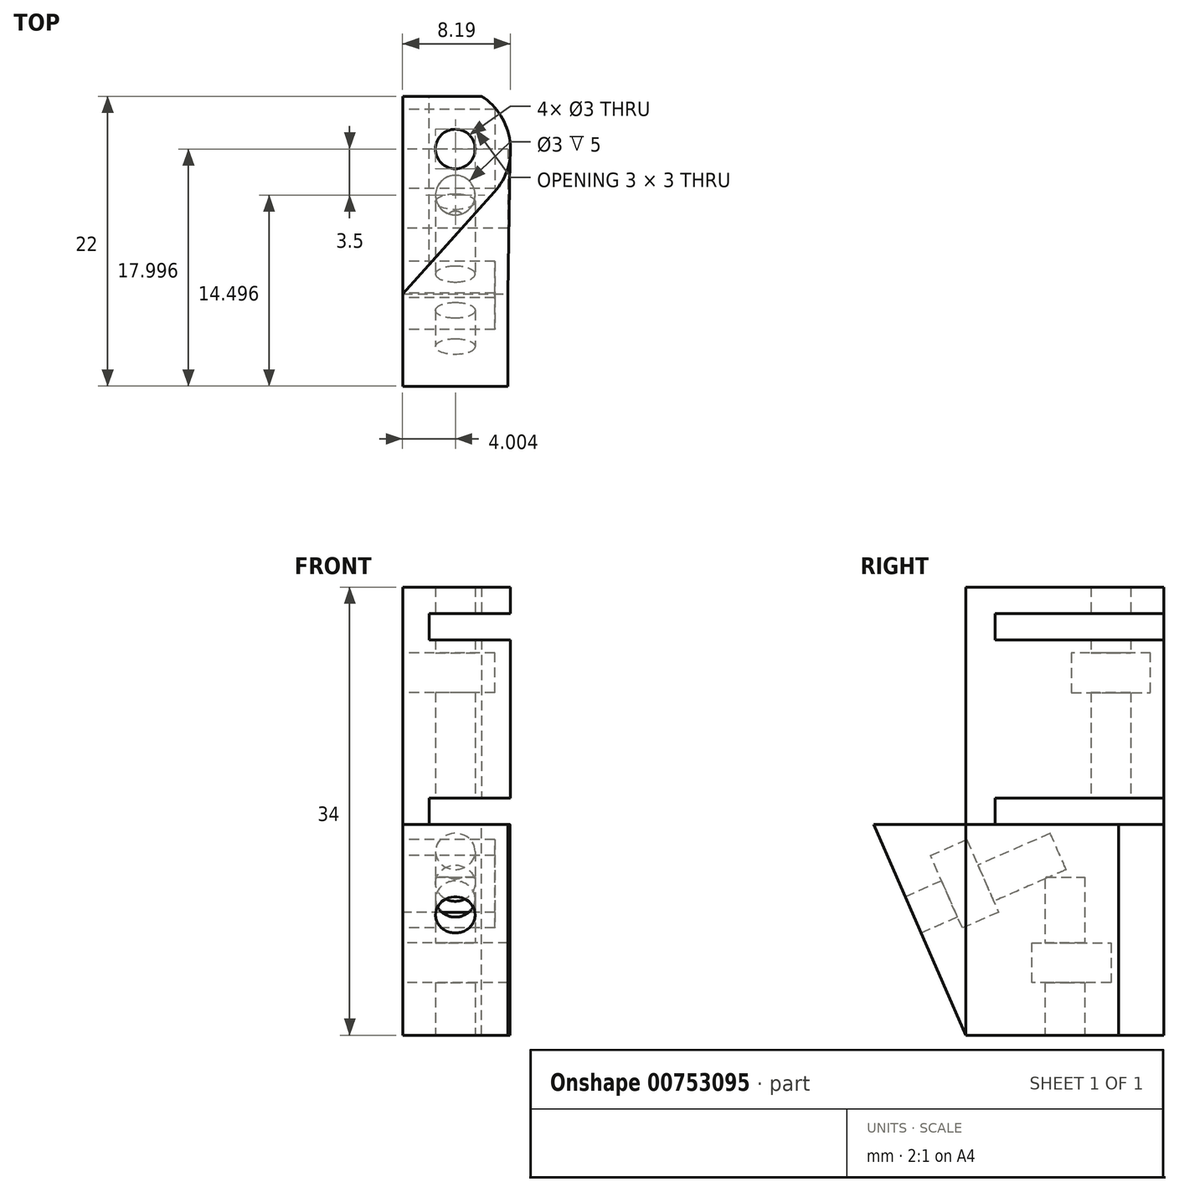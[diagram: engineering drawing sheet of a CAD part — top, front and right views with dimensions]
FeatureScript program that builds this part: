
annotation { "Feature Type Name" : "Feature", "Feature Type Description" : "" }
export const myFeature = defineFeature(function(context is Context, id is Id, definition is map)
    precondition{}
    {
        {
            var Q0;
            Q0=qCreatedBy(makeId("Top.planeOp"),FACE);
            var sketch = newSketch(context, id + "F0", { "sketchPlane" : qUnion([Q0])});
            skLineSegment(sketch, "E0", {"start": v(-26.19, -5.95) * mm, "end": v(-26.19, -20.95) * mm});
            skLineSegment(sketch, "E1", {"start": v(-26.19, -5.95) * mm, "end": v(-20.2, -5.95) * mm});
            skLineSegment(sketch, "E2", {"start": v(-26.19, -20.95) * mm, "end": v(-26.19, -14.95) * mm});
            skLineSegment(sketch, "E3", {"start": v(-26.19, -20.95) * mm, "end": v(-19.23, -13.23) * mm});
            skArc(sketch, "E4", {"start": v(-19.23, -13.23) * mm, "mid": v(-18.04, -9.37) * mm, "end": v(-20.2, -5.95) * mm});
            skCircle(sketch, "E5", {"center": v(-22.19, -9.95) * mm, "radius": 1.5 * mm});
            skSolve(sketch);
        }
        {
            var Q0;
            Q0=makeQuery(id+"F0.imprint","IMPRINT",FACE,{"disambiguationData":[TD([[makeQuery(id+"F0.imprint","IMPRINT",EDGE,{"derivedFrom":sQuery(id+"F0.wireOp",EDGE,"E0")}),1.0]])]});
            extrude(context, id + "F1", {"entities" : qUnion([Q0]), "depth" : 18 * mm, "offsetDistance" : 25 * mm});
        }
        {
            var Q0;
            Q0=makeQuery(id+"F1.opExtrude","SWEPT_FACE",FACE,{"disambiguationData":[OSD([sQuery(id+"F0.wireOp",EDGE,"E0"),sQuery(id+"F0.wireOp",EDGE,"E2")])]});
            var sketch = newSketch(context, id + "F2", { "sketchPlane" : qUnion([Q0])});
            skLineSegment(sketch, "E6", {"start": v(6.95, 13) * mm, "end": v(12.95, 13) * mm});
            skLineSegment(sketch, "E7", {"start": v(12.95, 13) * mm, "end": v(12.95, 10) * mm});
            skLineSegment(sketch, "E8", {"start": v(12.95, 10) * mm, "end": v(6.95, 10) * mm});
            skLineSegment(sketch, "E9", {"start": v(6.95, 10) * mm, "end": v(6.95, 13) * mm});
            skSolve(sketch);
        }
        {
            var Q0;
            Q0=makeQuery(id+"F2.imprint","IMPRINT",FACE,{"disambiguationData":[TD([[makeQuery(id+"F2.imprint","IMPRINT",EDGE,{"derivedFrom":sQuery(id+"F2.wireOp",EDGE,"E6")}),-1.0]])]});
            extrude(context, id + "F3", {"entities" : qUnion([Q0]), "operationType" : NewBodyOperationType.REMOVE, "oppositeDirection" : true, "depth" : 7 * mm, "offsetDistance" : 25 * mm});
        }
        {
            var Q0;
            Q0=makeQuery(id+"F1.opExtrude","CAP_FACE",FACE,{"disambiguationData":[OSD([sQuery(id+"F0.wireOp",EDGE,"E0"),sQuery(id+"F0.wireOp",EDGE,"E1"),sQuery(id+"F0.wireOp",EDGE,"E2"),sQuery(id+"F0.wireOp",EDGE,"E3"),sQuery(id+"F0.wireOp",EDGE,"E4"),sQuery(id+"F0.wireOp",EDGE,"E5")])],"isStart":true});
            var sketch = newSketch(context, id + "F4", { "sketchPlane" : qUnion([Q0])});
            skLineSegment(sketch, "E10", {"start": v(-26.19, 20.95) * mm, "end": v(-18.19, 20.95) * mm});
            skPoint(sketch, "E11.endSnap0", {"position": v(-18.04, 9.37) * mm});
            skLineSegment(sketch, "E12", {"start": v(-26.19, 20.95) * mm, "end": v(-26.19, 5.95) * mm});
            skLineSegment(sketch, "E13", {"start": v(-26.19, 5.95) * mm, "end": v(-20.2, 5.95) * mm});
            skArc(sketch, "E14", {"start": v(-20.2, 5.95) * mm, "mid": v(-18.74, 7.43) * mm, "end": v(-18.04, 9.37) * mm});
            skLineSegment(sketch, "E15", {"start": v(-18.19, 20.95) * mm, "end": v(-18.04, 9.37) * mm});
            skSolve(sketch);
        }
        {
            var Q0;
            Q0=makeQuery(id+"F4.imprint","IMPRINT",FACE,{"disambiguationData":[TD([[makeQuery(id+"F4.imprint","IMPRINT",EDGE,{"derivedFrom":sQuery(id+"F4.wireOp",EDGE,"E12")}),-1.0]])]});
            var Q1;
            {var subQ0=sQuery(id+"F4.wireOp",EDGE,"E10");Q1=makeQuery(id+"F4.imprint","IMPRINT",FACE,{"disambiguationData":[TD([[makeQuery(id+"F4.imprint","IMPRINT",EDGE,{"derivedFrom":subQ0}),-1.0]])]});}
            extrude(context, id + "F5", {"entities" : qUnion([Q0, Q1]), "operationType" : NewBodyOperationType.ADD, "depth" : 16 * mm, "offsetDistance" : 25 * mm});
        }
        {
            var Q0;
            Q0=makeQuery(id+"F5.opExtrude","CAP_FACE",FACE,{"disambiguationData":[OSD([sQuery(id+"F0.wireOp",EDGE,"E5"),sQuery(id+"F4.wireOp",EDGE,"E10"),sQuery(id+"F4.wireOp",EDGE,"E12"),sQuery(id+"F4.wireOp",EDGE,"E13"),sQuery(id+"F4.wireOp",EDGE,"E14"),sQuery(id+"F4.wireOp",EDGE,"E15")])],"isStart":false});
            var sketch = newSketch(context, id + "F6", { "sketchPlane" : qUnion([Q0])});
            skCircle(sketch, "E16", {"center": v(-22.19, 9.95) * mm, "radius": 1.5 * mm});
            skSolve(sketch);
        }
        {
            var Q0;
            Q0=qSketchRegion(id+"F6",true);
            extrude(context, id + "F7", {"entities" : qUnion([Q0]), "operationType" : NewBodyOperationType.ADD, "depth" : -16 * mm, "offsetDistance" : 25 * mm});
        }
        {
            var Q0;
            Q0=makeQuery(id+"F5.boolean.opBoolean","MERGE",FACE,{"derivedFrom":[makeQuery(id+"F1.opExtrude","SWEPT_FACE",FACE,{"disambiguationData":[OSD([sQuery(id+"F0.wireOp",EDGE,"E0"),sQuery(id+"F0.wireOp",EDGE,"E2")])]}),makeQuery(id+"F5.opExtrude","SWEPT_FACE",FACE,{"disambiguationData":[OSD([sQuery(id+"F4.wireOp",EDGE,"E12")])]})]});
            var sketch = newSketch(context, id + "F8", { "sketchPlane" : qUnion([Q0])});
            skLineSegment(sketch, "E17", {"start": v(20.95, -16) * mm, "end": v(20.95, 0) * mm});
            skLineSegment(sketch, "E18", {"start": v(20.95, 0) * mm, "end": v(27.95, 0) * mm});
            skLineSegment(sketch, "E19", {"start": v(27.95, 0) * mm, "end": v(20.95, -16) * mm});
            skSolve(sketch);
        }
        {
            var Q0;
            Q0=makeQuery(id+"F8.imprint","IMPRINT",FACE,{"disambiguationData":[TD([[makeQuery(id+"F8.imprint","IMPRINT",EDGE,{"derivedFrom":sQuery(id+"F8.wireOp",EDGE,"E17")}),-1.0]])]});
            extrude(context, id + "F9", {"entities" : qUnion([Q0]), "operationType" : NewBodyOperationType.ADD, "depth" : -8 * mm, "offsetDistance" : 25 * mm});
        }
        {
            var Q0;
            Q0=makeQuery(id+"F9.boolean.opBoolean","MERGE",FACE,{"derivedFrom":[makeQuery(id+"F5.boolean.opBoolean","MERGE",FACE,{"derivedFrom":[makeQuery(id+"F1.opExtrude","SWEPT_FACE",FACE,{"disambiguationData":[OSD([sQuery(id+"F0.wireOp",EDGE,"E0"),sQuery(id+"F0.wireOp",EDGE,"E2")])]}),makeQuery(id+"F5.opExtrude","SWEPT_FACE",FACE,{"disambiguationData":[OSD([sQuery(id+"F4.wireOp",EDGE,"E12")])]})]}),makeQuery(id+"F9.opExtrude","CAP_FACE",FACE,{"disambiguationData":[OSD([sQuery(id+"F8.wireOp",EDGE,"E17"),sQuery(id+"F8.wireOp",EDGE,"E18"),sQuery(id+"F8.wireOp",EDGE,"E19")])],"isStart":true})]});
            var sketch = newSketch(context, id + "F10", { "sketchPlane" : qUnion([Q0])});
            skLineSegment(sketch, "E20", {"start": v(23.64, -2.37) * mm, "end": v(20.9, -1.17) * mm});
            skLineSegment(sketch, "E21", {"start": v(20.9, -1.17) * mm, "end": v(18.48, -6.66) * mm});
            skLineSegment(sketch, "E22", {"start": v(18.48, -6.66) * mm, "end": v(21.23, -7.87) * mm});
            skLineSegment(sketch, "E23", {"start": v(21.23, -7.87) * mm, "end": v(23.64, -2.37) * mm});
            skSolve(sketch);
        }
        {
            var Q0;
            Q0=makeQuery(id+"F10.imprint","IMPRINT",FACE,{"disambiguationData":[TD([[makeQuery(id+"F10.imprint","IMPRINT",EDGE,{"derivedFrom":sQuery(id+"F10.wireOp",EDGE,"E20")}),1.0]])]});
            extrude(context, id + "F11", {"entities" : qUnion([Q0]), "operationType" : NewBodyOperationType.REMOVE, "oppositeDirection" : true, "depth" : 7 * mm, "offsetDistance" : 25 * mm});
        }
        {
            var Q0;
            Q0=makeQuery(id+"F9.opExtrude","SWEPT_FACE",FACE,{"disambiguationData":[OSD([sQuery(id+"F8.wireOp",EDGE,"E19")])]});
            var sketch = newSketch(context, id + "F12", { "sketchPlane" : qUnion([Q0])});
            skCircle(sketch, "E24", {"center": v(-22.19, 3.7) * mm, "radius": 1.5 * mm});
            skSolve(sketch);
        }
        {
            var Q0;
            Q0=makeQuery(id+"F12.imprint","IMPRINT",FACE,{"disambiguationData":[TD([[makeQuery(id+"F12.imprint","IMPRINT",EDGE,{"derivedFrom":sQuery(id+"F12.wireOp",EDGE,"E24")}),1.0]])]});
            extrude(context, id + "F13", {"entities" : qUnion([Q0]), "operationType" : NewBodyOperationType.REMOVE, "oppositeDirection" : true, "depth" : 12 * mm, "offsetDistance" : 25 * mm});
        }
        {
            var Q0;
            Q0=makeQuery(id+"F9.boolean.opBoolean","MERGE",FACE,{"derivedFrom":[makeQuery(id+"F5.boolean.opBoolean","MERGE",FACE,{"derivedFrom":[makeQuery(id+"F1.opExtrude","SWEPT_FACE",FACE,{"disambiguationData":[OSD([sQuery(id+"F0.wireOp",EDGE,"E0"),sQuery(id+"F0.wireOp",EDGE,"E2")])]}),makeQuery(id+"F5.opExtrude","SWEPT_FACE",FACE,{"disambiguationData":[OSD([sQuery(id+"F4.wireOp",EDGE,"E12")])]})]}),makeQuery(id+"F9.opExtrude","CAP_FACE",FACE,{"disambiguationData":[OSD([sQuery(id+"F8.wireOp",EDGE,"E17"),sQuery(id+"F8.wireOp",EDGE,"E18"),sQuery(id+"F8.wireOp",EDGE,"E19")])],"isStart":true})]});
            var sketch = newSketch(context, id + "F14", { "sketchPlane" : qUnion([Q0])});
            skLineSegment(sketch, "E25", {"start": v(9.95, -12) * mm, "end": v(15.95, -12) * mm});
            skLineSegment(sketch, "E26", {"start": v(15.95, -12) * mm, "end": v(15.95, -9) * mm});
            skLineSegment(sketch, "E27", {"start": v(15.95, -9) * mm, "end": v(9.95, -9) * mm});
            skLineSegment(sketch, "E28", {"start": v(9.95, -9) * mm, "end": v(9.95, -12) * mm});
            skSolve(sketch);
        }
        {
            var Q0;
            Q0=makeQuery(id+"F14.imprint","IMPRINT",FACE,{"disambiguationData":[TD([[makeQuery(id+"F14.imprint","IMPRINT",EDGE,{"derivedFrom":sQuery(id+"F14.wireOp",EDGE,"E25")}),1.0]])]});
            extrude(context, id + "F15", {"entities" : qUnion([Q0]), "operationType" : NewBodyOperationType.REMOVE, "oppositeDirection" : true, "depth" : 8 * mm, "offsetDistance" : 25 * mm});
        }
        {
            var Q0;
            Q0=makeQuery(id+"F7.boolean.opBoolean","MERGE",FACE,{"derivedFrom":[makeQuery(id+"F5.opExtrude","CAP_FACE",FACE,{"disambiguationData":[OSD([sQuery(id+"F0.wireOp",EDGE,"E5"),sQuery(id+"F4.wireOp",EDGE,"E10"),sQuery(id+"F4.wireOp",EDGE,"E12"),sQuery(id+"F4.wireOp",EDGE,"E13"),sQuery(id+"F4.wireOp",EDGE,"E14"),sQuery(id+"F4.wireOp",EDGE,"E15")])],"isStart":false}),makeQuery(id+"F7.opExtrude","CAP_FACE",FACE,{"disambiguationData":[OSD([sQuery(id+"F6.wireOp",EDGE,"E16")])],"isStart":true})]});
            var sketch = newSketch(context, id + "F16", { "sketchPlane" : qUnion([Q0])});
            skCircle(sketch, "E29", {"center": v(-22.19, 13.45) * mm, "radius": 1.5 * mm});
            skSolve(sketch);
        }
        {
            var Q0;
            Q0=makeQuery(id+"F16.imprint","IMPRINT",FACE,{"disambiguationData":[TD([[makeQuery(id+"F16.imprint","IMPRINT",EDGE,{"derivedFrom":sQuery(id+"F16.wireOp",EDGE,"E29")}),1.0]])]});
            extrude(context, id + "F17", {"entities" : qUnion([Q0]), "operationType" : NewBodyOperationType.REMOVE, "oppositeDirection" : true, "depth" : 12 * mm, "offsetDistance" : 25 * mm});
        }
        {
            var Q0;
            Q0=makeQuery(id+"F5.boolean.opBoolean","MERGE",FACE,{"derivedFrom":[makeQuery(id+"F1.opExtrude","SWEPT_FACE",FACE,{"disambiguationData":[OSD([sQuery(id+"F0.wireOp",EDGE,"E1")])]}),makeQuery(id+"F5.opExtrude","SWEPT_FACE",FACE,{"disambiguationData":[OSD([sQuery(id+"F4.wireOp",EDGE,"E13")])]})]});
            var sketch = newSketch(context, id + "F18", { "sketchPlane" : qUnion([Q0])});
            skLineSegment(sketch, "E30", {"start": v(26.19, 0) * mm, "end": v(24.19, 0) * mm});
            skLineSegment(sketch, "E31", {"start": v(24.19, 0) * mm, "end": v(24.19, 2) * mm});
            skLineSegment(sketch, "E32", {"start": v(24.19, 2) * mm, "end": v(26.19, 2) * mm});
            skLineSegment(sketch, "E33", {"start": v(24.19, 2) * mm, "end": v(20.2, 2) * mm});
            skLineSegment(sketch, "E34", {"start": v(20.2, 2) * mm, "end": v(20.2, 0) * mm});
            skLineSegment(sketch, "E35", {"start": v(20.2, 0) * mm, "end": v(24.19, 0) * mm});
            skSolve(sketch);
        }
        {
            var Q0;
            Q0=makeQuery(id+"F18.imprint","IMPRINT",FACE,{"disambiguationData":[TD([[makeQuery(id+"F18.imprint","IMPRINT",EDGE,{"derivedFrom":sQuery(id+"F18.wireOp",EDGE,"E31")}),1.0]])]});
            extrude(context, id + "F19", {"entities" : qUnion([Q0]), "operationType" : NewBodyOperationType.REMOVE, "oppositeDirection" : true, "depth" : 25 * mm, "offsetDistance" : 25 * mm});
        }
        {
            var Q0;
            Q0=makeQuery(id+"F19.boolean.opBoolean","COPY",FACE,{"derivedFrom":makeQuery(id+"F19.opExtrude","SWEPT_FACE",FACE,{"disambiguationData":[OSD([sQuery(id+"F18.wireOp",EDGE,"E34")])]})});
            extrude(context, id + "F20", {"entities" : qUnion([Q0]), "operationType" : NewBodyOperationType.REMOVE, "oppositeDirection" : true, "depth" : 25 * mm, "offsetDistance" : 25 * mm});
        }
        {
            var Q0;
            Q0=makeQuery(id+"F5.boolean.opBoolean","MERGE",FACE,{"derivedFrom":[makeQuery(id+"F1.opExtrude","SWEPT_FACE",FACE,{"disambiguationData":[OSD([sQuery(id+"F0.wireOp",EDGE,"E1")])]}),makeQuery(id+"F5.opExtrude","SWEPT_FACE",FACE,{"disambiguationData":[OSD([sQuery(id+"F4.wireOp",EDGE,"E13")])]})]});
            var sketch = newSketch(context, id + "F21", { "sketchPlane" : qUnion([Q0])});
            skLineSegment(sketch, "E36", {"start": v(26.19, 18) * mm, "end": v(26.19, 16) * mm});
            skLineSegment(sketch, "E37", {"start": v(26.19, 16) * mm, "end": v(26.19, 14) * mm});
            skLineSegment(sketch, "E38", {"start": v(26.19, 14) * mm, "end": v(24.19, 14) * mm});
            skLineSegment(sketch, "E39", {"start": v(24.19, 14) * mm, "end": v(20.2, 14) * mm});
            skLineSegment(sketch, "E40", {"start": v(20.2, 14) * mm, "end": v(20.2, 16) * mm});
            skLineSegment(sketch, "E41", {"start": v(20.2, 16) * mm, "end": v(26.19, 16) * mm});
            skLineSegment(sketch, "E42", {"start": v(24.19, 16) * mm, "end": v(24.19, 14) * mm});
            skSolve(sketch);
        }
        {
            var Q0;
            Q0=makeQuery(id+"F21.imprint","IMPRINT",FACE,{"disambiguationData":[TD([[makeQuery(id+"F21.imprint","IMPRINT",EDGE,{"derivedFrom":sQuery(id+"F21.wireOp",EDGE,"E39")}),-1.0]])]});
            extrude(context, id + "F22", {"entities" : qUnion([Q0]), "operationType" : NewBodyOperationType.REMOVE, "oppositeDirection" : true, "depth" : 25 * mm, "offsetDistance" : 25 * mm});
        }
        {
            var Q0;
            Q0=makeQuery(id+"F22.boolean.opBoolean","COPY",FACE,{"derivedFrom":makeQuery(id+"F22.opExtrude","SWEPT_FACE",FACE,{"disambiguationData":[OSD([sQuery(id+"F21.wireOp",EDGE,"E40")])]})});
            extrude(context, id + "F23", {"entities" : qUnion([Q0]), "operationType" : NewBodyOperationType.REMOVE, "oppositeDirection" : true, "depth" : 25 * mm, "offsetDistance" : 25 * mm});
        }
    });
